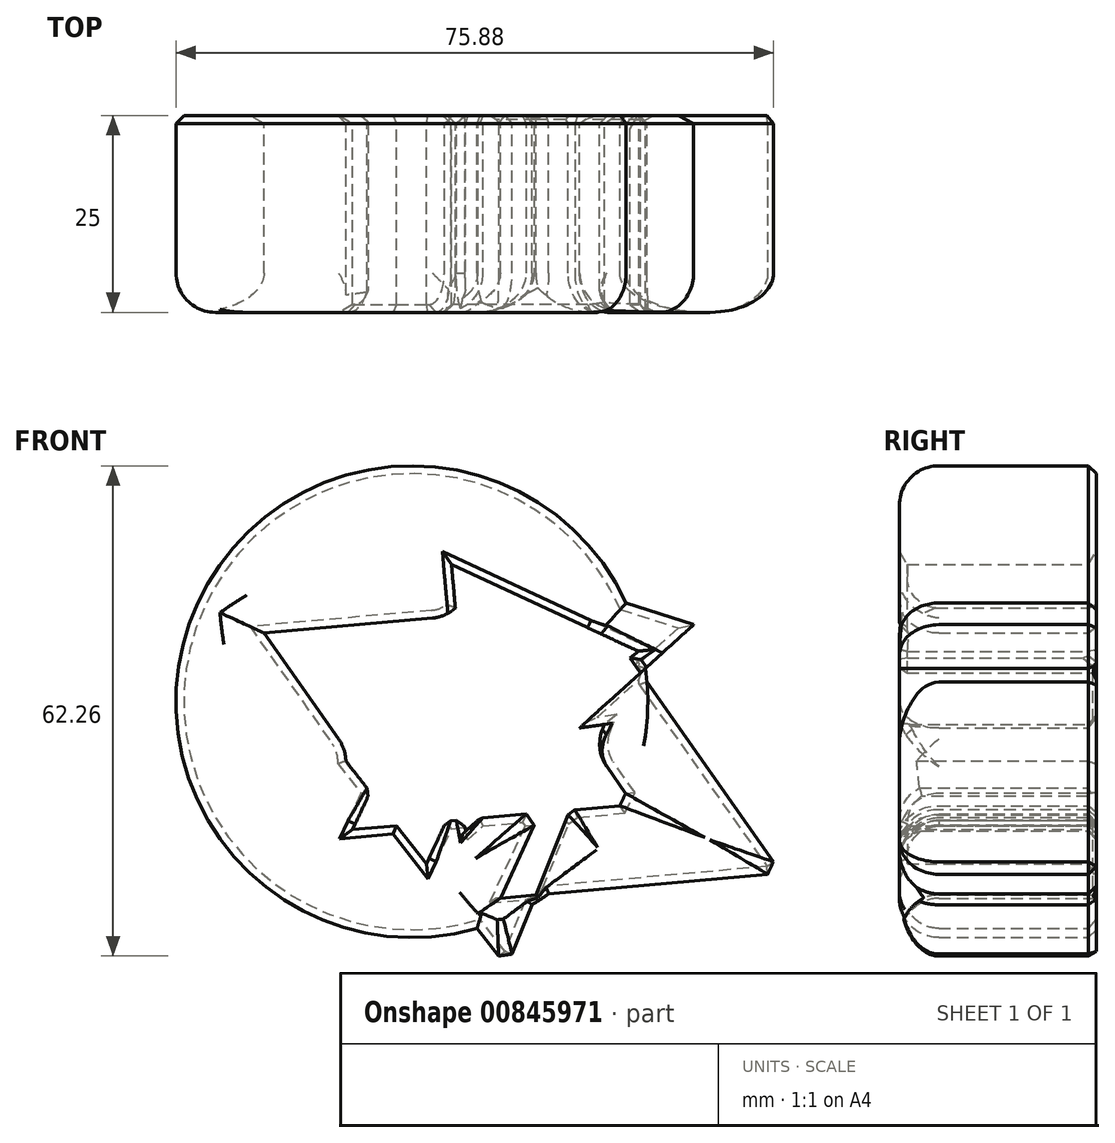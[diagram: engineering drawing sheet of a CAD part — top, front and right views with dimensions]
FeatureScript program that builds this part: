
annotation { "Feature Type Name" : "Feature", "Feature Type Description" : "" }
export const myFeature = defineFeature(function(context is Context, id is Id, definition is map)
    precondition{}
    {
        {
            var Q0;
            Q0=qCreatedBy(makeId("Front.planeOp"),FACE);
            var sketch = newSketch(context, id + "F0", { "sketchPlane" : qUnion([Q0])});
            skCircle(sketch, "E0", {"center": v(0, 0) * mm, "radius": 29.96 * mm});
            skCircle(sketch, "E1.cCircle", {"center": v(0, 0) * mm, "radius": 10.34 * mm, "construction": true});
            skLineSegment(sketch, "E1.0", {"start": v(16.92, 11.9) * mm, "end": v(1.84, -20.6) * mm});
            skLineSegment(sketch, "E1.1", {"start": v(1.84, -20.6) * mm, "end": v(-18.77, 8.7) * mm});
            skLineSegment(sketch, "E1.2", {"start": v(-18.77, 8.7) * mm, "end": v(16.92, 11.9) * mm});
            skPoint(sketch, "E1.0.midPoint", {"position": v(9.38, -4.35) * mm});
            skCircle(sketch, "E2.cCircle", {"center": v(9.38, -4.35) * mm, "radius": 10.34 * mm, "construction": true});
            skLineSegment(sketch, "E2.0", {"start": v(-7.54, -16.25) * mm, "end": v(7.54, 16.25) * mm});
            skLineSegment(sketch, "E2.1", {"start": v(7.54, 16.25) * mm, "end": v(28.15, -13.06) * mm});
            skLineSegment(sketch, "E2.2", {"start": v(28.15, -13.06) * mm, "end": v(-7.54, -16.25) * mm});
            skCircle(sketch, "E3.cCircle", {"center": v(28.15, -13.06) * mm, "radius": 10.34 * mm, "construction": true});
            skLineSegment(sketch, "E3.0", {"start": v(11.23, -24.96) * mm, "end": v(26.3, 7.55) * mm});
            skLineSegment(sketch, "E3.1", {"start": v(26.3, 7.55) * mm, "end": v(46.92, -21.77) * mm});
            skLineSegment(sketch, "E3.2", {"start": v(46.92, -21.77) * mm, "end": v(11.23, -24.96) * mm});
            skPoint(sketch, "E3.0.midPoint", {"position": v(18.77, -8.7) * mm});
            skCircle(sketch, "E4.cCircle", {"center": v(9.38, -14.7) * mm, "radius": 9.58 * mm, "construction": true});
            skLineSegment(sketch, "E4.0", {"start": v(12.08, -33.67) * mm, "end": v(-8.4, -7.55) * mm});
            skLineSegment(sketch, "E4.1", {"start": v(-8.4, -7.55) * mm, "end": v(24.47, -2.88) * mm});
            skLineSegment(sketch, "E4.2", {"start": v(24.47, -2.88) * mm, "end": v(12.08, -33.67) * mm});
            skPoint(sketch, "E4.0.midPoint", {"position": v(1.84, -20.6) * mm});
            skCircle(sketch, "E5.cCircle", {"center": v(13.74, 5.03) * mm, "radius": 7.57 * mm, "construction": true});
            skLineSegment(sketch, "E5.0", {"start": v(5.03, 17.42) * mm, "end": v(28.82, 6.38) * mm});
            skLineSegment(sketch, "E5.1", {"start": v(28.82, 6.38) * mm, "end": v(7.36, -8.7) * mm});
            skLineSegment(sketch, "E5.2", {"start": v(7.36, -8.7) * mm, "end": v(5.03, 17.42) * mm});
            skPoint(sketch, "E5.0.midPoint", {"position": v(16.92, 11.9) * mm});
            skCircle(sketch, "E6.cCircle", {"center": v(13.74, 5.03) * mm, "radius": 11.28 * mm, "construction": true});
            skLineSegment(sketch, "E6.0", {"start": v(35.79, 9.79) * mm, "end": v(6.83, -16.44) * mm});
            skLineSegment(sketch, "E6.1", {"start": v(6.83, -16.44) * mm, "end": v(-1.4, 21.75) * mm});
            skLineSegment(sketch, "E6.2", {"start": v(-1.4, 21.75) * mm, "end": v(35.79, 9.79) * mm});
            skPoint(sketch, "E6.0.midPoint", {"position": v(21.3, -3.33) * mm});
            skSolve(sketch);
        }
        {
            var Q0;
            Q0 = qSketchRegion(id + "F0", true);
            extrude(context, id + "F1", {"entities" : qUnion([Q0]), "depth" : 25 * mm, "offsetDistance" : 25 * mm});
        }
        {
            var Q0;
            {var subQ0=sQuery(id+"F0.wireOp",EDGE,"E0");Q0=makeQuery(id+"F1.opExtrude","CAP_EDGE",EDGE,{"disambiguationData":[OSD([subQ0]),TDD([makeQuery(id+"F0.imprint","IMPRINT",EDGE,{"disambiguationData":[TD([[makeQuery(id+"F0.imprint","INTERSECT",VERTEX,{"derivedFrom":[subQ0,sQuery(id+"F0.wireOp",EDGE,"E6.2")]}),-1.0]])],"derivedFrom":subQ0})])],"isStart":false});}
            var Q1;
            {var subQ0=sQuery(id+"F0.wireOp",EDGE,"E3.2");Q1=makeQuery(id+"F1.opExtrude","CAP_EDGE",EDGE,{"disambiguationData":[OSD([subQ0]),TDD([makeQuery(id+"F0.imprint","IMPRINT",EDGE,{"disambiguationData":[TD([[makeQuery(id+"F0.imprint","INTERSECT",VERTEX,{"derivedFrom":[sQuery(id+"F0.wireOp",EDGE,"E3.1"),subQ0]}),-1.0]])],"derivedFrom":subQ0})])],"isStart":false});}
            var Q2;
            {var subQ0=sQuery(id+"F0.wireOp",EDGE,"E4.2");Q2=makeQuery(id+"F1.opExtrude","CAP_EDGE",EDGE,{"disambiguationData":[OSD([subQ0]),TDD([makeQuery(id+"F0.imprint","IMPRINT",EDGE,{"disambiguationData":[TD([[makeQuery(id+"F0.imprint","INTERSECT",VERTEX,{"derivedFrom":[sQuery(id+"F0.wireOp",EDGE,"E4.0"),subQ0]}),1.0]])],"derivedFrom":subQ0})])],"isStart":false});}
            var Q3;
            {var subQ0=sQuery(id+"F0.wireOp",EDGE,"E0");Q3=makeQuery(id+"F1.opExtrude","CAP_EDGE",EDGE,{"disambiguationData":[OSD([subQ0]),TDD([makeQuery(id+"F0.imprint","IMPRINT",EDGE,{"disambiguationData":[TD([[makeQuery(id+"F0.imprint","INTERSECT",VERTEX,{"derivedFrom":[subQ0,sQuery(id+"F0.wireOp",EDGE,"E4.2")]}),-1.0]])],"derivedFrom":subQ0})])],"isStart":false});}
            var Q4;
            {var subQ0=sQuery(id+"F0.wireOp",EDGE,"E4.0");Q4=makeQuery(id+"F1.opExtrude","CAP_EDGE",EDGE,{"disambiguationData":[OSD([subQ0]),TDD([makeQuery(id+"F0.imprint","IMPRINT",EDGE,{"disambiguationData":[TD([[makeQuery(id+"F0.imprint","INTERSECT",VERTEX,{"derivedFrom":[subQ0,sQuery(id+"F0.wireOp",EDGE,"E4.2")]}),-1.0]])],"derivedFrom":subQ0})])],"isStart":false});}
            var Q5;
            Q5=makeQuery(id+"F1.opExtrude","CAP_EDGE",EDGE,{"disambiguationData":[OSD([sQuery(id+"F0.wireOp",EDGE,"E6.2")])],"isStart":false});
            var Q6;
            {var subQ0=sQuery(id+"F0.wireOp",EDGE,"E3.1");Q6=makeQuery(id+"F1.opExtrude","CAP_EDGE",EDGE,{"disambiguationData":[OSD([subQ0]),TDD([makeQuery(id+"F0.imprint","IMPRINT",EDGE,{"disambiguationData":[TD([[makeQuery(id+"F0.imprint","INTERSECT",VERTEX,{"derivedFrom":[subQ0,sQuery(id+"F0.wireOp",EDGE,"E3.2")]}),1.0]])],"derivedFrom":subQ0})])],"isStart":false});}
            var Q7;
            Q7=makeQuery(id+"F1.opExtrude","CAP_EDGE",EDGE,{"disambiguationData":[OSD([sQuery(id+"F0.wireOp",EDGE,"E1.1")])],"isStart":false});
            var Q8;
            Q8=makeQuery(id+"F1.opExtrude","CAP_EDGE",EDGE,{"disambiguationData":[OSD([sQuery(id+"F0.wireOp",EDGE,"E1.2")])],"isStart":false});
            var Q9;
            Q9=makeQuery(id+"F1.opExtrude","SWEPT_EDGE",EDGE,{"disambiguationData":[OSD([sQuery(id+"F0.wireOp",EDGE,"E1.2"),sQuery(id+"F0.wireOp",EDGE,"E2.0")])]});
            var Q10;
            Q10=makeQuery(id+"F1.opExtrude","SWEPT_EDGE",EDGE,{"disambiguationData":[OSD([sQuery(id+"F0.wireOp",EDGE,"E1.1"),sQuery(id+"F0.wireOp",EDGE,"E4.1")])]});
            var Q11;
            Q11=makeQuery(id+"F1.opExtrude","SWEPT_EDGE",EDGE,{"disambiguationData":[OSD([sQuery(id+"F0.wireOp",EDGE,"E2.1"),sQuery(id+"F0.wireOp",EDGE,"E4.2")])]});
            var Q12;
            Q12=makeQuery(id+"F1.opExtrude","CAP_EDGE",EDGE,{"disambiguationData":[OSD([sQuery(id+"F0.wireOp",EDGE,"E2.1")])],"isStart":false});
            var Q13;
            {var subQ0=sQuery(id+"F0.wireOp",EDGE,"E2.2");var subQ1=makeQuery(id+"F0.imprint","INTERSECT",VERTEX,{"derivedFrom":[sQuery(id+"F0.wireOp",EDGE,"E0"),subQ0]});Q13=makeQuery(id+"F1.opExtrude","CAP_EDGE",EDGE,{"disambiguationData":[OSD([subQ0]),TDD([makeQuery(id+"F0.imprint","IMPRINT",EDGE,{"disambiguationData":[TD([[makeQuery(id+"F0.imprint","INTERSECT",VERTEX,{"derivedFrom":[sQuery(id+"F0.wireOp",EDGE,"E2.1"),subQ0]}),-1.0]])],"derivedFrom":subQ0}),makeQuery(id+"F0.imprint","IMPRINT",EDGE,{"disambiguationData":[TD([[subQ1,-1.0]])],"derivedFrom":subQ0})])],"isStart":false});}
            var Q14;
            {var subQ0=sQuery(id+"F0.wireOp",EDGE,"E4.2");Q14=makeQuery(id+"F1.opExtrude","CAP_EDGE",EDGE,{"disambiguationData":[OSD([subQ0]),TDD([makeQuery(id+"F0.imprint","IMPRINT",EDGE,{"disambiguationData":[TD([[makeQuery(id+"F0.imprint","INTERSECT",VERTEX,{"derivedFrom":[sQuery(id+"F0.wireOp",EDGE,"E2.2"),subQ0]}),-1.0]])],"derivedFrom":subQ0})])],"isStart":false});}
            var Q15;
            {var subQ0=sQuery(id+"F0.wireOp",EDGE,"E3.2");Q15=makeQuery(id+"F1.opExtrude","CAP_EDGE",EDGE,{"disambiguationData":[OSD([subQ0]),TDD([makeQuery(id+"F0.imprint","IMPRINT",EDGE,{"disambiguationData":[TD([[makeQuery(id+"F0.imprint","INTERSECT",VERTEX,{"derivedFrom":[sQuery(id+"F0.wireOp",EDGE,"E3.0"),subQ0]}),1.0]])],"derivedFrom":subQ0})])],"isStart":false});}
            var Q16;
            Q16=makeQuery(id+"F1.opExtrude","CAP_EDGE",EDGE,{"disambiguationData":[OSD([sQuery(id+"F0.wireOp",EDGE,"E3.0")])],"isStart":false});
            var Q17;
            {var subQ0=sQuery(id+"F0.wireOp",EDGE,"E2.2");Q17=makeQuery(id+"F1.opExtrude","CAP_EDGE",EDGE,{"disambiguationData":[OSD([subQ0]),TDD([makeQuery(id+"F0.imprint","IMPRINT",EDGE,{"disambiguationData":[TD([[makeQuery(id+"F0.imprint","INTERSECT",VERTEX,{"derivedFrom":[subQ0,sQuery(id+"F0.wireOp",EDGE,"E3.0")]}),-1.0]])],"derivedFrom":subQ0})])],"isStart":false});}
            fillet(context, id + "F2", {"entities" : qUnion([Q0, Q1, Q2, Q3, Q4, Q5, Q6, Q7, Q8, Q9, Q10, Q11, Q12, Q13, Q14, Q15, Q16, Q17]), "radius" : 5 * mm, "tangentPropagation" : true, "allowEdgeOverflow" : false});
        }
        {
            var Q0;
            Q0=makeQuery(id+"F1.opExtrude","CAP_EDGE",EDGE,{"disambiguationData":[OSD([sQuery(id+"F0.wireOp",EDGE,"E5.0")])],"isStart":false});
            var Q1;
            Q1=makeQuery(id+"F1.opExtrude","CAP_EDGE",EDGE,{"disambiguationData":[OSD([sQuery(id+"F0.wireOp",EDGE,"E5.1")])],"isStart":false});
            var Q2;
            {var subQ0=sQuery(id+"F0.wireOp",EDGE,"E3.1");Q2=makeQuery(id+"F1.opExtrude","CAP_EDGE",EDGE,{"disambiguationData":[OSD([subQ0]),TDD([makeQuery(id+"F0.imprint","IMPRINT",EDGE,{"disambiguationData":[TD([[makeQuery(id+"F0.imprint","INTERSECT",VERTEX,{"derivedFrom":[subQ0,sQuery(id+"F0.wireOp",EDGE,"E5.1")]}),-1.0]])],"derivedFrom":subQ0})])],"isStart":false});}
            var Q3;
            Q3=makeQuery(id+"F2.opFillet","BLEND_EDGE",EDGE,{"blendedFrom":[makeQuery(id+"F1.opExtrude","CAP_EDGE",EDGE,{"disambiguationData":[OSD([sQuery(id+"F0.wireOp",EDGE,"E1.2")])],"isStart":false}),makeQuery(id+"F1.opExtrude","SWEPT_FACE",FACE,{"disambiguationData":[OSD([sQuery(id+"F0.wireOp",EDGE,"E5.2")])]})],"blendedInto":[makeQuery(id+"F1.opExtrude","SWEPT_FACE",FACE,{"disambiguationData":[OSD([sQuery(id+"F0.wireOp",EDGE,"E5.2")])]})]});
            var Q4;
            Q4=makeQuery(id+"F1.opExtrude","CAP_EDGE",EDGE,{"disambiguationData":[OSD([sQuery(id+"F0.wireOp",EDGE,"E5.2")])],"isStart":false});
            var Q5;
            {var subQ0=sQuery(id+"F0.wireOp",EDGE,"E2.2");Q5=makeQuery(id+"F1.opExtrude","CAP_EDGE",EDGE,{"disambiguationData":[OSD([subQ0]),TDD([makeQuery(id+"F0.imprint","IMPRINT",EDGE,{"disambiguationData":[TD([[makeQuery(id+"F0.imprint","INTERSECT",VERTEX,{"derivedFrom":[sQuery(id+"F0.wireOp",EDGE,"E2.0"),subQ0]}),1.0]])],"derivedFrom":subQ0})])],"isStart":false});}
            var Q6;
            {var subQ0=sQuery(id+"F0.wireOp",EDGE,"E2.0");Q6=makeQuery(id+"F2.opFillet","BLEND_EDGE",EDGE,{"blendedFrom":[makeQuery(id+"F1.opExtrude","CAP_EDGE",EDGE,{"disambiguationData":[OSD([sQuery(id+"F0.wireOp",EDGE,"E1.1")])],"isStart":false}),makeQuery(id+"F1.opExtrude","SWEPT_FACE",FACE,{"disambiguationData":[OSD([subQ0]),TDD([makeQuery(id+"F0.imprint","IMPRINT",EDGE,{"disambiguationData":[TD([[makeQuery(id+"F0.imprint","INTERSECT",VERTEX,{"derivedFrom":[subQ0,sQuery(id+"F0.wireOp",EDGE,"E2.2")]}),-1.0]])],"derivedFrom":subQ0})])]})],"blendedInto":[makeQuery(id+"F1.opExtrude","SWEPT_FACE",FACE,{"disambiguationData":[OSD([subQ0]),TDD([makeQuery(id+"F0.imprint","IMPRINT",EDGE,{"disambiguationData":[TD([[makeQuery(id+"F0.imprint","INTERSECT",VERTEX,{"derivedFrom":[subQ0,sQuery(id+"F0.wireOp",EDGE,"E2.2")]}),-1.0]])],"derivedFrom":subQ0})])]})]});}
            var Q7;
            {var subQ0=sQuery(id+"F0.wireOp",EDGE,"E4.0");Q7=makeQuery(id+"F1.opExtrude","CAP_EDGE",EDGE,{"disambiguationData":[OSD([subQ0]),TDD([makeQuery(id+"F0.imprint","IMPRINT",EDGE,{"disambiguationData":[TD([[makeQuery(id+"F0.imprint","INTERSECT",VERTEX,{"derivedFrom":[sQuery(id+"F0.wireOp",EDGE,"E2.2"),subQ0]}),1.0]])],"derivedFrom":subQ0})])],"isStart":false});}
            var Q8;
            {var subQ0=sQuery(id+"F0.wireOp",EDGE,"E2.2");Q8=makeQuery(id+"F2.opFillet","BLEND_EDGE",EDGE,{"blendedFrom":[makeQuery(id+"F1.opExtrude","CAP_EDGE",EDGE,{"disambiguationData":[OSD([subQ0]),TDD([makeQuery(id+"F0.imprint","IMPRINT",EDGE,{"disambiguationData":[TD([[makeQuery(id+"F0.imprint","INTERSECT",VERTEX,{"derivedFrom":[subQ0,sQuery(id+"F0.wireOp",EDGE,"E3.0")]}),-1.0]])],"derivedFrom":subQ0})])],"isStart":false}),makeQuery(id+"F1.opExtrude","SWEPT_FACE",FACE,{"disambiguationData":[OSD([sQuery(id+"F0.wireOp",EDGE,"E1.0")])]})],"blendedInto":[makeQuery(id+"F1.opExtrude","SWEPT_FACE",FACE,{"disambiguationData":[OSD([sQuery(id+"F0.wireOp",EDGE,"E1.0")])]})]});}
            var Q9;
            {var subQ0=sQuery(id+"F0.wireOp",EDGE,"E6.0");var subQ1=sQuery(id+"F0.wireOp",EDGE,"E2.2");Q9=makeQuery(id+"F2.opFillet","BLEND_EDGE",EDGE,{"blendedFrom":[makeQuery(id+"F1.opExtrude","CAP_EDGE",EDGE,{"disambiguationData":[OSD([subQ1]),TDD([makeQuery(id+"F0.imprint","IMPRINT",EDGE,{"disambiguationData":[TD([[makeQuery(id+"F0.imprint","INTERSECT",VERTEX,{"derivedFrom":[subQ1,sQuery(id+"F0.wireOp",EDGE,"E3.0")]}),-1.0]])],"derivedFrom":subQ1})])],"isStart":false}),makeQuery(id+"F1.opExtrude","SWEPT_FACE",FACE,{"disambiguationData":[OSD([subQ0]),TDD([makeQuery(id+"F0.imprint","IMPRINT",EDGE,{"disambiguationData":[TD([[makeQuery(id+"F0.imprint","INTERSECT",VERTEX,{"derivedFrom":[subQ0,sQuery(id+"F0.wireOp",EDGE,"E6.1")]}),1.0]])],"derivedFrom":subQ0})])]})],"blendedInto":[makeQuery(id+"F1.opExtrude","SWEPT_FACE",FACE,{"disambiguationData":[OSD([subQ0]),TDD([makeQuery(id+"F0.imprint","IMPRINT",EDGE,{"disambiguationData":[TD([[makeQuery(id+"F0.imprint","INTERSECT",VERTEX,{"derivedFrom":[subQ0,sQuery(id+"F0.wireOp",EDGE,"E6.1")]}),1.0]])],"derivedFrom":subQ0})])]})]});}
            var Q10;
            {var subQ0=sQuery(id+"F0.wireOp",EDGE,"E2.2");Q10=makeQuery(id+"F2.opFillet","BLEND_EDGE",EDGE,{"blendedFrom":[makeQuery(id+"F1.opExtrude","CAP_EDGE",EDGE,{"disambiguationData":[OSD([subQ0]),TDD([makeQuery(id+"F0.imprint","IMPRINT",EDGE,{"disambiguationData":[TD([[makeQuery(id+"F0.imprint","INTERSECT",VERTEX,{"derivedFrom":[subQ0,sQuery(id+"F0.wireOp",EDGE,"E3.0")]}),-1.0]])],"derivedFrom":subQ0})])],"isStart":false}),makeQuery(id+"F1.opExtrude","SWEPT_FACE",FACE,{"disambiguationData":[OSD([sQuery(id+"F0.wireOp",EDGE,"E6.1")])]})],"blendedInto":[makeQuery(id+"F1.opExtrude","SWEPT_FACE",FACE,{"disambiguationData":[OSD([sQuery(id+"F0.wireOp",EDGE,"E6.1")])]})]});}
            var Q11;
            Q11=makeQuery(id+"F1.opExtrude","SWEPT_EDGE",EDGE,{"disambiguationData":[OSD([sQuery(id+"F0.wireOp",EDGE,"E2.2"),sQuery(id+"F0.wireOp",EDGE,"E3.0")])]});
            var Q12;
            {var subQ0=sQuery(id+"F0.wireOp",EDGE,"E3.0");var subQ1=sQuery(id+"F0.wireOp",EDGE,"E2.2");Q12=makeQuery(id+"F2.opFillet","BLEND_EDGE",EDGE,{"blendedFrom":[makeQuery(id+"F1.opExtrude","CAP_EDGE",EDGE,{"disambiguationData":[OSD([subQ1]),TDD([makeQuery(id+"F0.imprint","IMPRINT",EDGE,{"disambiguationData":[TD([[makeQuery(id+"F0.imprint","INTERSECT",VERTEX,{"derivedFrom":[subQ1,subQ0]}),-1.0]])],"derivedFrom":subQ1})])],"isStart":false}),makeQuery(id+"F1.opExtrude","CAP_EDGE",EDGE,{"disambiguationData":[OSD([subQ0])],"isStart":false})],"blendedInto":[]});}
            var Q13;
            Q13=makeQuery(id+"F1.opExtrude","SWEPT_EDGE",EDGE,{"disambiguationData":[OSD([sQuery(id+"F0.wireOp",EDGE,"E2.2"),sQuery(id+"F0.wireOp",EDGE,"E4.2")])]});
            var Q14;
            {var subQ0=sQuery(id+"F0.wireOp",EDGE,"E4.2");var subQ1=sQuery(id+"F0.wireOp",EDGE,"E2.2");var subQ2=makeQuery(id+"F0.imprint","INTERSECT",VERTEX,{"derivedFrom":[subQ1,subQ0]});var subQ3=makeQuery(id+"F0.imprint","INTERSECT",VERTEX,{"derivedFrom":[sQuery(id+"F0.wireOp",EDGE,"E0"),subQ1]});Q14=makeQuery(id+"F2.opFillet","BLEND_EDGE",EDGE,{"blendedFrom":[makeQuery(id+"F1.opExtrude","CAP_EDGE",EDGE,{"disambiguationData":[OSD([subQ1]),TDD([makeQuery(id+"F0.imprint","IMPRINT",EDGE,{"disambiguationData":[TD([[makeQuery(id+"F0.imprint","INTERSECT",VERTEX,{"derivedFrom":[sQuery(id+"F0.wireOp",EDGE,"E2.1"),subQ1]}),-1.0]])],"derivedFrom":subQ1}),makeQuery(id+"F0.imprint","IMPRINT",EDGE,{"disambiguationData":[TD([[subQ3,-1.0]])],"derivedFrom":subQ1})])],"isStart":false}),makeQuery(id+"F1.opExtrude","CAP_EDGE",EDGE,{"disambiguationData":[OSD([subQ0]),TDD([makeQuery(id+"F0.imprint","IMPRINT",EDGE,{"disambiguationData":[TD([[subQ2,-1.0]])],"derivedFrom":subQ0})])],"isStart":false})],"blendedInto":[]});}
            var Q15;
            Q15=makeQuery(id+"F1.opExtrude","SWEPT_EDGE",EDGE,{"disambiguationData":[OSD([sQuery(id+"F0.wireOp",EDGE,"E2.1"),sQuery(id+"F0.wireOp",EDGE,"E2.2")])]});
            var Q16;
            {var subQ0=sQuery(id+"F0.wireOp",EDGE,"E2.1");Q16=makeQuery(id+"F2.opFillet","BLEND_EDGE",EDGE,{"blendedFrom":[makeQuery(id+"F1.opExtrude","SWEPT_EDGE",EDGE,{"disambiguationData":[OSD([subQ0,sQuery(id+"F0.wireOp",EDGE,"E4.2")])]}),makeQuery(id+"F1.opExtrude","CAP_EDGE",EDGE,{"disambiguationData":[OSD([subQ0])],"isStart":false})],"blendedInto":[]});}
            var Q17;
            Q17=makeQuery(id+"F1.opExtrude","SWEPT_EDGE",EDGE,{"disambiguationData":[OSD([sQuery(id+"F0.wireOp",EDGE,"E2.0"),sQuery(id+"F0.wireOp",EDGE,"E4.0")])]});
            var Q18;
            {var subQ0=sQuery(id+"F0.wireOp",EDGE,"E1.1");Q18=makeQuery(id+"F2.opFillet","BLEND_EDGE",EDGE,{"blendedFrom":[makeQuery(id+"F1.opExtrude","SWEPT_EDGE",EDGE,{"disambiguationData":[OSD([subQ0,sQuery(id+"F0.wireOp",EDGE,"E4.1")])]}),makeQuery(id+"F1.opExtrude","SWEPT_FACE",FACE,{"disambiguationData":[OSD([subQ0])]})],"blendedInto":[makeQuery(id+"F1.opExtrude","SWEPT_FACE",FACE,{"disambiguationData":[OSD([subQ0])]})]});}
            chamfer(context, id + "F3", {"entities" : qUnion([Q0, Q1, Q2, Q3, Q4, Q5, Q6, Q7, Q8, Q9, Q10, Q11, Q12, Q13, Q14, Q15, Q16, Q17, Q18]), "width" : 1 * mm, "tangentPropagation" : true});
        }
        {
            var Q0;
            {var subQ0=sQuery(id+"F0.wireOp",EDGE,"E0");Q0=makeQuery(id+"F1.opExtrude","CAP_EDGE",EDGE,{"disambiguationData":[OSD([subQ0]),TDD([makeQuery(id+"F0.imprint","IMPRINT",EDGE,{"disambiguationData":[TD([[makeQuery(id+"F0.imprint","INTERSECT",VERTEX,{"derivedFrom":[subQ0,sQuery(id+"F0.wireOp",EDGE,"E6.2")]}),-1.0]])],"derivedFrom":subQ0})])],"isStart":true});}
            var Q1;
            {var subQ0=sQuery(id+"F0.wireOp",EDGE,"E3.1");Q1=makeQuery(id+"F1.opExtrude","CAP_EDGE",EDGE,{"disambiguationData":[OSD([subQ0]),TDD([makeQuery(id+"F0.imprint","IMPRINT",EDGE,{"disambiguationData":[TD([[makeQuery(id+"F0.imprint","INTERSECT",VERTEX,{"derivedFrom":[subQ0,sQuery(id+"F0.wireOp",EDGE,"E3.2")]}),1.0]])],"derivedFrom":subQ0})])],"isStart":true});}
            var Q2;
            {var subQ0=sQuery(id+"F0.wireOp",EDGE,"E3.2");Q2=makeQuery(id+"F1.opExtrude","CAP_EDGE",EDGE,{"disambiguationData":[OSD([subQ0]),TDD([makeQuery(id+"F0.imprint","IMPRINT",EDGE,{"disambiguationData":[TD([[makeQuery(id+"F0.imprint","INTERSECT",VERTEX,{"derivedFrom":[sQuery(id+"F0.wireOp",EDGE,"E3.1"),subQ0]}),-1.0]])],"derivedFrom":subQ0})])],"isStart":true});}
            var Q3;
            {var subQ0=sQuery(id+"F0.wireOp",EDGE,"E0");Q3=makeQuery(id+"F1.opExtrude","CAP_EDGE",EDGE,{"disambiguationData":[OSD([subQ0]),TDD([makeQuery(id+"F0.imprint","IMPRINT",EDGE,{"disambiguationData":[TD([[makeQuery(id+"F0.imprint","INTERSECT",VERTEX,{"derivedFrom":[subQ0,sQuery(id+"F0.wireOp",EDGE,"E4.2")]}),-1.0]])],"derivedFrom":subQ0})])],"isStart":true});}
            var Q4;
            {var subQ0=sQuery(id+"F0.wireOp",EDGE,"E4.2");Q4=makeQuery(id+"F1.opExtrude","CAP_EDGE",EDGE,{"disambiguationData":[OSD([subQ0]),TDD([makeQuery(id+"F0.imprint","IMPRINT",EDGE,{"disambiguationData":[TD([[makeQuery(id+"F0.imprint","INTERSECT",VERTEX,{"derivedFrom":[sQuery(id+"F0.wireOp",EDGE,"E4.0"),subQ0]}),1.0]])],"derivedFrom":subQ0})])],"isStart":true});}
            var Q5;
            {var subQ0=sQuery(id+"F0.wireOp",EDGE,"E4.0");Q5=makeQuery(id+"F1.opExtrude","CAP_EDGE",EDGE,{"disambiguationData":[OSD([subQ0]),TDD([makeQuery(id+"F0.imprint","IMPRINT",EDGE,{"disambiguationData":[TD([[makeQuery(id+"F0.imprint","INTERSECT",VERTEX,{"derivedFrom":[subQ0,sQuery(id+"F0.wireOp",EDGE,"E4.2")]}),-1.0]])],"derivedFrom":subQ0})])],"isStart":true});}
            var Q6;
            Q6=makeQuery(id+"F1.opExtrude","CAP_EDGE",EDGE,{"disambiguationData":[OSD([sQuery(id+"F0.wireOp",EDGE,"E6.2")])],"isStart":true});
            var Q7;
            {var subQ0=sQuery(id+"F0.wireOp",EDGE,"E6.0");Q7=makeQuery(id+"F1.opExtrude","CAP_EDGE",EDGE,{"disambiguationData":[OSD([subQ0]),TDD([makeQuery(id+"F0.imprint","IMPRINT",EDGE,{"disambiguationData":[TD([[makeQuery(id+"F0.imprint","INTERSECT",VERTEX,{"derivedFrom":[subQ0,sQuery(id+"F0.wireOp",EDGE,"E6.2")]}),-1.0]])],"derivedFrom":subQ0})])],"isStart":true});}
            var Q8;
            {var subQ0=sQuery(id+"F0.wireOp",EDGE,"E0");Q8=makeQuery(id+"F1.opExtrude","CAP_EDGE",EDGE,{"disambiguationData":[OSD([subQ0]),TDD([makeQuery(id+"F0.imprint","IMPRINT",EDGE,{"disambiguationData":[TD([[makeQuery(id+"F0.imprint","INTERSECT",VERTEX,{"derivedFrom":[subQ0,sQuery(id+"F0.wireOp",EDGE,"E6.0")]}),1.0]])],"derivedFrom":subQ0})])],"isStart":true});}
            var Q9;
            Q9=makeQuery(id+"F1.opExtrude","CAP_EDGE",EDGE,{"disambiguationData":[OSD([sQuery(id+"F0.wireOp",EDGE,"E5.0")])],"isStart":true});
            var Q10;
            Q10=makeQuery(id+"F1.opExtrude","CAP_EDGE",EDGE,{"disambiguationData":[OSD([sQuery(id+"F0.wireOp",EDGE,"E5.2")])],"isStart":true});
            var Q11;
            Q11=makeQuery(id+"F1.opExtrude","CAP_EDGE",EDGE,{"disambiguationData":[OSD([sQuery(id+"F0.wireOp",EDGE,"E1.2")])],"isStart":true});
            var Q12;
            {var subQ0=sQuery(id+"F0.wireOp",EDGE,"E2.0");var subQ1=sQuery(id+"F0.wireOp",EDGE,"E1.2");Q12=makeQuery(id+"F2.opFillet","BLEND_EDGE",EDGE,{"blendedFrom":[makeQuery(id+"F1.opExtrude","SWEPT_EDGE",EDGE,{"disambiguationData":[OSD([subQ1,subQ0])]}),makeQuery(id+"F1.opExtrude","CAP_FACE",FACE,{"disambiguationData":[OSD([sQuery(id+"F0.wireOp",EDGE,"E0"),sQuery(id+"F0.wireOp",EDGE,"E1.0"),sQuery(id+"F0.wireOp",EDGE,"E1.1"),subQ1,subQ0,sQuery(id+"F0.wireOp",EDGE,"E2.1"),sQuery(id+"F0.wireOp",EDGE,"E2.2"),sQuery(id+"F0.wireOp",EDGE,"E3.0"),sQuery(id+"F0.wireOp",EDGE,"E3.1"),sQuery(id+"F0.wireOp",EDGE,"E3.2"),sQuery(id+"F0.wireOp",EDGE,"E4.0"),sQuery(id+"F0.wireOp",EDGE,"E4.1"),sQuery(id+"F0.wireOp",EDGE,"E4.2"),sQuery(id+"F0.wireOp",EDGE,"E5.0"),sQuery(id+"F0.wireOp",EDGE,"E5.1"),sQuery(id+"F0.wireOp",EDGE,"E5.2"),sQuery(id+"F0.wireOp",EDGE,"E6.0"),sQuery(id+"F0.wireOp",EDGE,"E6.1"),sQuery(id+"F0.wireOp",EDGE,"E6.2")])],"isStart":true})],"blendedInto":[makeQuery(id+"F1.opExtrude","CAP_FACE",FACE,{"disambiguationData":[OSD([sQuery(id+"F0.wireOp",EDGE,"E0"),sQuery(id+"F0.wireOp",EDGE,"E1.0"),sQuery(id+"F0.wireOp",EDGE,"E1.1"),subQ1,subQ0,sQuery(id+"F0.wireOp",EDGE,"E2.1"),sQuery(id+"F0.wireOp",EDGE,"E2.2"),sQuery(id+"F0.wireOp",EDGE,"E3.0"),sQuery(id+"F0.wireOp",EDGE,"E3.1"),sQuery(id+"F0.wireOp",EDGE,"E3.2"),sQuery(id+"F0.wireOp",EDGE,"E4.0"),sQuery(id+"F0.wireOp",EDGE,"E4.1"),sQuery(id+"F0.wireOp",EDGE,"E4.2"),sQuery(id+"F0.wireOp",EDGE,"E5.0"),sQuery(id+"F0.wireOp",EDGE,"E5.1"),sQuery(id+"F0.wireOp",EDGE,"E5.2"),sQuery(id+"F0.wireOp",EDGE,"E6.0"),sQuery(id+"F0.wireOp",EDGE,"E6.1"),sQuery(id+"F0.wireOp",EDGE,"E6.2")])],"isStart":true})]});}
            var Q13;
            Q13=makeQuery(id+"F1.opExtrude","CAP_EDGE",EDGE,{"disambiguationData":[OSD([sQuery(id+"F0.wireOp",EDGE,"E1.1")])],"isStart":true});
            var Q14;
            {var subQ0=sQuery(id+"F0.wireOp",EDGE,"E4.0");Q14=makeQuery(id+"F1.opExtrude","CAP_EDGE",EDGE,{"disambiguationData":[OSD([subQ0]),TDD([makeQuery(id+"F0.imprint","IMPRINT",EDGE,{"disambiguationData":[TD([[makeQuery(id+"F0.imprint","INTERSECT",VERTEX,{"derivedFrom":[subQ0,sQuery(id+"F0.wireOp",EDGE,"E4.1")]}),1.0]])],"derivedFrom":subQ0})])],"isStart":true});}
            var Q15;
            {var subQ0=sQuery(id+"F0.wireOp",EDGE,"E4.1");var subQ1=sQuery(id+"F0.wireOp",EDGE,"E1.1");Q15=makeQuery(id+"F2.opFillet","BLEND_EDGE",EDGE,{"blendedFrom":[makeQuery(id+"F1.opExtrude","SWEPT_EDGE",EDGE,{"disambiguationData":[OSD([subQ1,subQ0])]}),makeQuery(id+"F1.opExtrude","CAP_FACE",FACE,{"disambiguationData":[OSD([sQuery(id+"F0.wireOp",EDGE,"E0"),sQuery(id+"F0.wireOp",EDGE,"E1.0"),subQ1,sQuery(id+"F0.wireOp",EDGE,"E1.2"),sQuery(id+"F0.wireOp",EDGE,"E2.0"),sQuery(id+"F0.wireOp",EDGE,"E2.1"),sQuery(id+"F0.wireOp",EDGE,"E2.2"),sQuery(id+"F0.wireOp",EDGE,"E3.0"),sQuery(id+"F0.wireOp",EDGE,"E3.1"),sQuery(id+"F0.wireOp",EDGE,"E3.2"),sQuery(id+"F0.wireOp",EDGE,"E4.0"),subQ0,sQuery(id+"F0.wireOp",EDGE,"E4.2"),sQuery(id+"F0.wireOp",EDGE,"E5.0"),sQuery(id+"F0.wireOp",EDGE,"E5.1"),sQuery(id+"F0.wireOp",EDGE,"E5.2"),sQuery(id+"F0.wireOp",EDGE,"E6.0"),sQuery(id+"F0.wireOp",EDGE,"E6.1"),sQuery(id+"F0.wireOp",EDGE,"E6.2")])],"isStart":true})],"blendedInto":[makeQuery(id+"F1.opExtrude","CAP_FACE",FACE,{"disambiguationData":[OSD([sQuery(id+"F0.wireOp",EDGE,"E0"),sQuery(id+"F0.wireOp",EDGE,"E1.0"),subQ1,sQuery(id+"F0.wireOp",EDGE,"E1.2"),sQuery(id+"F0.wireOp",EDGE,"E2.0"),sQuery(id+"F0.wireOp",EDGE,"E2.1"),sQuery(id+"F0.wireOp",EDGE,"E2.2"),sQuery(id+"F0.wireOp",EDGE,"E3.0"),sQuery(id+"F0.wireOp",EDGE,"E3.1"),sQuery(id+"F0.wireOp",EDGE,"E3.2"),sQuery(id+"F0.wireOp",EDGE,"E4.0"),subQ0,sQuery(id+"F0.wireOp",EDGE,"E4.2"),sQuery(id+"F0.wireOp",EDGE,"E5.0"),sQuery(id+"F0.wireOp",EDGE,"E5.1"),sQuery(id+"F0.wireOp",EDGE,"E5.2"),sQuery(id+"F0.wireOp",EDGE,"E6.0"),sQuery(id+"F0.wireOp",EDGE,"E6.1"),sQuery(id+"F0.wireOp",EDGE,"E6.2")])],"isStart":true})]});}
            var Q16;
            {var subQ0=sQuery(id+"F0.wireOp",EDGE,"E2.0");Q16=makeQuery(id+"F1.opExtrude","CAP_EDGE",EDGE,{"disambiguationData":[OSD([subQ0]),TDD([makeQuery(id+"F0.imprint","IMPRINT",EDGE,{"disambiguationData":[TD([[makeQuery(id+"F0.imprint","INTERSECT",VERTEX,{"derivedFrom":[subQ0,sQuery(id+"F0.wireOp",EDGE,"E2.2")]}),-1.0]])],"derivedFrom":subQ0})])],"isStart":true});}
            var Q17;
            {var subQ0=sQuery(id+"F0.wireOp",EDGE,"E2.2");Q17=makeQuery(id+"F1.opExtrude","CAP_EDGE",EDGE,{"disambiguationData":[OSD([subQ0]),TDD([makeQuery(id+"F0.imprint","IMPRINT",EDGE,{"disambiguationData":[TD([[makeQuery(id+"F0.imprint","INTERSECT",VERTEX,{"derivedFrom":[sQuery(id+"F0.wireOp",EDGE,"E2.0"),subQ0]}),1.0]])],"derivedFrom":subQ0})])],"isStart":true});}
            var Q18;
            {var subQ0=sQuery(id+"F0.wireOp",EDGE,"E4.0");Q18=makeQuery(id+"F1.opExtrude","CAP_EDGE",EDGE,{"disambiguationData":[OSD([subQ0]),TDD([makeQuery(id+"F0.imprint","IMPRINT",EDGE,{"disambiguationData":[TD([[makeQuery(id+"F0.imprint","INTERSECT",VERTEX,{"derivedFrom":[sQuery(id+"F0.wireOp",EDGE,"E2.2"),subQ0]}),1.0]])],"derivedFrom":subQ0})])],"isStart":true});}
            var Q19;
            Q19=makeQuery(id+"F1.opExtrude","CAP_EDGE",EDGE,{"disambiguationData":[OSD([sQuery(id+"F0.wireOp",EDGE,"E3.0")])],"isStart":true});
            var Q20;
            {var subQ0=sQuery(id+"F0.wireOp",EDGE,"E3.0");var subQ1=sQuery(id+"F0.wireOp",EDGE,"E2.2");Q20=makeQuery(id+"F3.opChamfer","BLEND_EDGE",EDGE,{"blendedFrom":[makeQuery(id+"F1.opExtrude","SWEPT_EDGE",EDGE,{"disambiguationData":[OSD([subQ1,subQ0])]}),makeQuery(id+"F1.opExtrude","CAP_FACE",FACE,{"disambiguationData":[OSD([sQuery(id+"F0.wireOp",EDGE,"E0"),sQuery(id+"F0.wireOp",EDGE,"E1.0"),sQuery(id+"F0.wireOp",EDGE,"E1.1"),sQuery(id+"F0.wireOp",EDGE,"E1.2"),sQuery(id+"F0.wireOp",EDGE,"E2.0"),sQuery(id+"F0.wireOp",EDGE,"E2.1"),subQ1,subQ0,sQuery(id+"F0.wireOp",EDGE,"E3.1"),sQuery(id+"F0.wireOp",EDGE,"E3.2"),sQuery(id+"F0.wireOp",EDGE,"E4.0"),sQuery(id+"F0.wireOp",EDGE,"E4.1"),sQuery(id+"F0.wireOp",EDGE,"E4.2"),sQuery(id+"F0.wireOp",EDGE,"E5.0"),sQuery(id+"F0.wireOp",EDGE,"E5.1"),sQuery(id+"F0.wireOp",EDGE,"E5.2"),sQuery(id+"F0.wireOp",EDGE,"E6.0"),sQuery(id+"F0.wireOp",EDGE,"E6.1"),sQuery(id+"F0.wireOp",EDGE,"E6.2")])],"isStart":true})],"blendedInto":[makeQuery(id+"F1.opExtrude","CAP_FACE",FACE,{"disambiguationData":[OSD([sQuery(id+"F0.wireOp",EDGE,"E0"),sQuery(id+"F0.wireOp",EDGE,"E1.0"),sQuery(id+"F0.wireOp",EDGE,"E1.1"),sQuery(id+"F0.wireOp",EDGE,"E1.2"),sQuery(id+"F0.wireOp",EDGE,"E2.0"),sQuery(id+"F0.wireOp",EDGE,"E2.1"),subQ1,subQ0,sQuery(id+"F0.wireOp",EDGE,"E3.1"),sQuery(id+"F0.wireOp",EDGE,"E3.2"),sQuery(id+"F0.wireOp",EDGE,"E4.0"),sQuery(id+"F0.wireOp",EDGE,"E4.1"),sQuery(id+"F0.wireOp",EDGE,"E4.2"),sQuery(id+"F0.wireOp",EDGE,"E5.0"),sQuery(id+"F0.wireOp",EDGE,"E5.1"),sQuery(id+"F0.wireOp",EDGE,"E5.2"),sQuery(id+"F0.wireOp",EDGE,"E6.0"),sQuery(id+"F0.wireOp",EDGE,"E6.1"),sQuery(id+"F0.wireOp",EDGE,"E6.2")])],"isStart":true})]});}
            var Q21;
            {var subQ0=sQuery(id+"F0.wireOp",EDGE,"E2.2");Q21=makeQuery(id+"F1.opExtrude","CAP_EDGE",EDGE,{"disambiguationData":[OSD([subQ0]),TDD([makeQuery(id+"F0.imprint","IMPRINT",EDGE,{"disambiguationData":[TD([[makeQuery(id+"F0.imprint","INTERSECT",VERTEX,{"derivedFrom":[subQ0,sQuery(id+"F0.wireOp",EDGE,"E3.0")]}),-1.0]])],"derivedFrom":subQ0})])],"isStart":true});}
            var Q22;
            {var subQ0=sQuery(id+"F0.wireOp",EDGE,"E6.0");Q22=makeQuery(id+"F1.opExtrude","CAP_EDGE",EDGE,{"disambiguationData":[OSD([subQ0]),TDD([makeQuery(id+"F0.imprint","IMPRINT",EDGE,{"disambiguationData":[TD([[makeQuery(id+"F0.imprint","INTERSECT",VERTEX,{"derivedFrom":[subQ0,sQuery(id+"F0.wireOp",EDGE,"E6.1")]}),1.0]])],"derivedFrom":subQ0})])],"isStart":true});}
            var Q23;
            Q23=makeQuery(id+"F1.opExtrude","CAP_EDGE",EDGE,{"disambiguationData":[OSD([sQuery(id+"F0.wireOp",EDGE,"E1.0")])],"isStart":true});
            var Q24;
            {var subQ0=sQuery(id+"F0.wireOp",EDGE,"E2.2");Q24=makeQuery(id+"F1.opExtrude","CAP_EDGE",EDGE,{"disambiguationData":[OSD([subQ0]),TDD([makeQuery(id+"F0.imprint","IMPRINT",EDGE,{"disambiguationData":[TD([[makeQuery(id+"F0.imprint","INTERSECT",VERTEX,{"derivedFrom":[sQuery(id+"F0.wireOp",EDGE,"E1.0"),subQ0]}),1.0]])],"derivedFrom":subQ0})])],"isStart":true});}
            var Q25;
            {var subQ0=sQuery(id+"F0.wireOp",EDGE,"E2.2");var subQ1=makeQuery(id+"F0.imprint","INTERSECT",VERTEX,{"derivedFrom":[sQuery(id+"F0.wireOp",EDGE,"E0"),subQ0]});Q25=makeQuery(id+"F1.opExtrude","CAP_EDGE",EDGE,{"disambiguationData":[OSD([subQ0]),TDD([makeQuery(id+"F0.imprint","IMPRINT",EDGE,{"disambiguationData":[TD([[makeQuery(id+"F0.imprint","INTERSECT",VERTEX,{"derivedFrom":[sQuery(id+"F0.wireOp",EDGE,"E2.1"),subQ0]}),-1.0]])],"derivedFrom":subQ0}),makeQuery(id+"F0.imprint","IMPRINT",EDGE,{"disambiguationData":[TD([[subQ1,-1.0]])],"derivedFrom":subQ0})])],"isStart":true});}
            var Q26;
            {var subQ0=sQuery(id+"F0.wireOp",EDGE,"E2.2");var subQ1=sQuery(id+"F0.wireOp",EDGE,"E2.1");Q26=makeQuery(id+"F3.opChamfer","BLEND_EDGE",EDGE,{"blendedFrom":[makeQuery(id+"F1.opExtrude","SWEPT_EDGE",EDGE,{"disambiguationData":[OSD([subQ1,subQ0])]}),makeQuery(id+"F1.opExtrude","CAP_FACE",FACE,{"disambiguationData":[OSD([sQuery(id+"F0.wireOp",EDGE,"E0"),sQuery(id+"F0.wireOp",EDGE,"E1.0"),sQuery(id+"F0.wireOp",EDGE,"E1.1"),sQuery(id+"F0.wireOp",EDGE,"E1.2"),sQuery(id+"F0.wireOp",EDGE,"E2.0"),subQ1,subQ0,sQuery(id+"F0.wireOp",EDGE,"E3.0"),sQuery(id+"F0.wireOp",EDGE,"E3.1"),sQuery(id+"F0.wireOp",EDGE,"E3.2"),sQuery(id+"F0.wireOp",EDGE,"E4.0"),sQuery(id+"F0.wireOp",EDGE,"E4.1"),sQuery(id+"F0.wireOp",EDGE,"E4.2"),sQuery(id+"F0.wireOp",EDGE,"E5.0"),sQuery(id+"F0.wireOp",EDGE,"E5.1"),sQuery(id+"F0.wireOp",EDGE,"E5.2"),sQuery(id+"F0.wireOp",EDGE,"E6.0"),sQuery(id+"F0.wireOp",EDGE,"E6.1"),sQuery(id+"F0.wireOp",EDGE,"E6.2")])],"isStart":true})],"blendedInto":[makeQuery(id+"F1.opExtrude","CAP_FACE",FACE,{"disambiguationData":[OSD([sQuery(id+"F0.wireOp",EDGE,"E0"),sQuery(id+"F0.wireOp",EDGE,"E1.0"),sQuery(id+"F0.wireOp",EDGE,"E1.1"),sQuery(id+"F0.wireOp",EDGE,"E1.2"),sQuery(id+"F0.wireOp",EDGE,"E2.0"),subQ1,subQ0,sQuery(id+"F0.wireOp",EDGE,"E3.0"),sQuery(id+"F0.wireOp",EDGE,"E3.1"),sQuery(id+"F0.wireOp",EDGE,"E3.2"),sQuery(id+"F0.wireOp",EDGE,"E4.0"),sQuery(id+"F0.wireOp",EDGE,"E4.1"),sQuery(id+"F0.wireOp",EDGE,"E4.2"),sQuery(id+"F0.wireOp",EDGE,"E5.0"),sQuery(id+"F0.wireOp",EDGE,"E5.1"),sQuery(id+"F0.wireOp",EDGE,"E5.2"),sQuery(id+"F0.wireOp",EDGE,"E6.0"),sQuery(id+"F0.wireOp",EDGE,"E6.1"),sQuery(id+"F0.wireOp",EDGE,"E6.2")])],"isStart":true})]});}
            var Q27;
            {var subQ0=sQuery(id+"F0.wireOp",EDGE,"E4.2");var subQ1=sQuery(id+"F0.wireOp",EDGE,"E2.2");Q27=makeQuery(id+"F3.opChamfer","BLEND_EDGE",EDGE,{"blendedFrom":[makeQuery(id+"F1.opExtrude","SWEPT_EDGE",EDGE,{"disambiguationData":[OSD([subQ1,subQ0])]}),makeQuery(id+"F1.opExtrude","CAP_FACE",FACE,{"disambiguationData":[OSD([sQuery(id+"F0.wireOp",EDGE,"E0"),sQuery(id+"F0.wireOp",EDGE,"E1.0"),sQuery(id+"F0.wireOp",EDGE,"E1.1"),sQuery(id+"F0.wireOp",EDGE,"E1.2"),sQuery(id+"F0.wireOp",EDGE,"E2.0"),sQuery(id+"F0.wireOp",EDGE,"E2.1"),subQ1,sQuery(id+"F0.wireOp",EDGE,"E3.0"),sQuery(id+"F0.wireOp",EDGE,"E3.1"),sQuery(id+"F0.wireOp",EDGE,"E3.2"),sQuery(id+"F0.wireOp",EDGE,"E4.0"),sQuery(id+"F0.wireOp",EDGE,"E4.1"),subQ0,sQuery(id+"F0.wireOp",EDGE,"E5.0"),sQuery(id+"F0.wireOp",EDGE,"E5.1"),sQuery(id+"F0.wireOp",EDGE,"E5.2"),sQuery(id+"F0.wireOp",EDGE,"E6.0"),sQuery(id+"F0.wireOp",EDGE,"E6.1"),sQuery(id+"F0.wireOp",EDGE,"E6.2")])],"isStart":true})],"blendedInto":[makeQuery(id+"F1.opExtrude","CAP_FACE",FACE,{"disambiguationData":[OSD([sQuery(id+"F0.wireOp",EDGE,"E0"),sQuery(id+"F0.wireOp",EDGE,"E1.0"),sQuery(id+"F0.wireOp",EDGE,"E1.1"),sQuery(id+"F0.wireOp",EDGE,"E1.2"),sQuery(id+"F0.wireOp",EDGE,"E2.0"),sQuery(id+"F0.wireOp",EDGE,"E2.1"),subQ1,sQuery(id+"F0.wireOp",EDGE,"E3.0"),sQuery(id+"F0.wireOp",EDGE,"E3.1"),sQuery(id+"F0.wireOp",EDGE,"E3.2"),sQuery(id+"F0.wireOp",EDGE,"E4.0"),sQuery(id+"F0.wireOp",EDGE,"E4.1"),subQ0,sQuery(id+"F0.wireOp",EDGE,"E5.0"),sQuery(id+"F0.wireOp",EDGE,"E5.1"),sQuery(id+"F0.wireOp",EDGE,"E5.2"),sQuery(id+"F0.wireOp",EDGE,"E6.0"),sQuery(id+"F0.wireOp",EDGE,"E6.1"),sQuery(id+"F0.wireOp",EDGE,"E6.2")])],"isStart":true})]});}
            var Q28;
            Q28=makeQuery(id+"F1.opExtrude","CAP_EDGE",EDGE,{"disambiguationData":[OSD([sQuery(id+"F0.wireOp",EDGE,"E2.1")])],"isStart":true});
            var Q29;
            {var subQ0=sQuery(id+"F0.wireOp",EDGE,"E4.2");var subQ1=sQuery(id+"F0.wireOp",EDGE,"E2.1");Q29=makeQuery(id+"F2.opFillet","BLEND_EDGE",EDGE,{"blendedFrom":[makeQuery(id+"F1.opExtrude","SWEPT_EDGE",EDGE,{"disambiguationData":[OSD([subQ1,subQ0])]}),makeQuery(id+"F1.opExtrude","CAP_FACE",FACE,{"disambiguationData":[OSD([sQuery(id+"F0.wireOp",EDGE,"E0"),sQuery(id+"F0.wireOp",EDGE,"E1.0"),sQuery(id+"F0.wireOp",EDGE,"E1.1"),sQuery(id+"F0.wireOp",EDGE,"E1.2"),sQuery(id+"F0.wireOp",EDGE,"E2.0"),subQ1,sQuery(id+"F0.wireOp",EDGE,"E2.2"),sQuery(id+"F0.wireOp",EDGE,"E3.0"),sQuery(id+"F0.wireOp",EDGE,"E3.1"),sQuery(id+"F0.wireOp",EDGE,"E3.2"),sQuery(id+"F0.wireOp",EDGE,"E4.0"),sQuery(id+"F0.wireOp",EDGE,"E4.1"),subQ0,sQuery(id+"F0.wireOp",EDGE,"E5.0"),sQuery(id+"F0.wireOp",EDGE,"E5.1"),sQuery(id+"F0.wireOp",EDGE,"E5.2"),sQuery(id+"F0.wireOp",EDGE,"E6.0"),sQuery(id+"F0.wireOp",EDGE,"E6.1"),sQuery(id+"F0.wireOp",EDGE,"E6.2")])],"isStart":true})],"blendedInto":[makeQuery(id+"F1.opExtrude","CAP_FACE",FACE,{"disambiguationData":[OSD([sQuery(id+"F0.wireOp",EDGE,"E0"),sQuery(id+"F0.wireOp",EDGE,"E1.0"),sQuery(id+"F0.wireOp",EDGE,"E1.1"),sQuery(id+"F0.wireOp",EDGE,"E1.2"),sQuery(id+"F0.wireOp",EDGE,"E2.0"),subQ1,sQuery(id+"F0.wireOp",EDGE,"E2.2"),sQuery(id+"F0.wireOp",EDGE,"E3.0"),sQuery(id+"F0.wireOp",EDGE,"E3.1"),sQuery(id+"F0.wireOp",EDGE,"E3.2"),sQuery(id+"F0.wireOp",EDGE,"E4.0"),sQuery(id+"F0.wireOp",EDGE,"E4.1"),subQ0,sQuery(id+"F0.wireOp",EDGE,"E5.0"),sQuery(id+"F0.wireOp",EDGE,"E5.1"),sQuery(id+"F0.wireOp",EDGE,"E5.2"),sQuery(id+"F0.wireOp",EDGE,"E6.0"),sQuery(id+"F0.wireOp",EDGE,"E6.1"),sQuery(id+"F0.wireOp",EDGE,"E6.2")])],"isStart":true})]});}
            var Q30;
            {var subQ0=sQuery(id+"F0.wireOp",EDGE,"E4.2");Q30=makeQuery(id+"F1.opExtrude","CAP_EDGE",EDGE,{"disambiguationData":[OSD([subQ0]),TDD([makeQuery(id+"F0.imprint","IMPRINT",EDGE,{"disambiguationData":[TD([[makeQuery(id+"F0.imprint","INTERSECT",VERTEX,{"derivedFrom":[sQuery(id+"F0.wireOp",EDGE,"E4.1"),subQ0]}),-1.0]])],"derivedFrom":subQ0})])],"isStart":true});}
            var Q31;
            {var subQ0=sQuery(id+"F0.wireOp",EDGE,"E4.1");Q31=makeQuery(id+"F1.opExtrude","CAP_EDGE",EDGE,{"disambiguationData":[OSD([subQ0]),TDD([makeQuery(id+"F0.imprint","IMPRINT",EDGE,{"disambiguationData":[TD([[makeQuery(id+"F0.imprint","INTERSECT",VERTEX,{"derivedFrom":[subQ0,sQuery(id+"F0.wireOp",EDGE,"E4.2")]}),1.0]])],"derivedFrom":subQ0})])],"isStart":true});}
            var Q32;
            Q32=makeQuery(id+"F1.opExtrude","CAP_EDGE",EDGE,{"disambiguationData":[OSD([sQuery(id+"F0.wireOp",EDGE,"E5.1")])],"isStart":true});
            var Q33;
            Q33=makeQuery(id+"F1.opExtrude","SWEPT_EDGE",EDGE,{"disambiguationData":[OSD([sQuery(id+"F0.wireOp",EDGE,"E3.1"),sQuery(id+"F0.wireOp",EDGE,"E3.2")])]});
            var Q34;
            Q34=makeQuery(id+"F1.opExtrude","SWEPT_EDGE",EDGE,{"disambiguationData":[OSD([sQuery(id+"F0.wireOp",EDGE,"E4.0"),sQuery(id+"F0.wireOp",EDGE,"E4.2")])]});
            chamfer(context, id + "F4", {"entities" : qUnion([Q0, Q1, Q2, Q3, Q4, Q5, Q6, Q7, Q8, Q9, Q10, Q11, Q12, Q13, Q14, Q15, Q16, Q17, Q18, Q19, Q20, Q21, Q22, Q23, Q24, Q25, Q26, Q27, Q28, Q29, Q30, Q31, Q32, Q33, Q34]), "width" : 1 * mm, "tangentPropagation" : true});
        }
        {
            var Q0;
            {var subQ0=sQuery(id+"F0.wireOp",EDGE,"E6.0");Q0=makeQuery(id+"F1.opExtrude","CAP_EDGE",EDGE,{"disambiguationData":[OSD([subQ0]),TDD([makeQuery(id+"F0.imprint","IMPRINT",EDGE,{"disambiguationData":[TD([[makeQuery(id+"F0.imprint","INTERSECT",VERTEX,{"derivedFrom":[sQuery(id+"F0.wireOp",EDGE,"E3.1"),subQ0]}),-1.0]])],"derivedFrom":subQ0})])],"isStart":true});}
            var Q1;
            {var subQ0=sQuery(id+"F0.wireOp",EDGE,"E3.1");Q1=makeQuery(id+"F1.opExtrude","CAP_EDGE",EDGE,{"disambiguationData":[OSD([subQ0]),TDD([makeQuery(id+"F0.imprint","IMPRINT",EDGE,{"disambiguationData":[TD([[makeQuery(id+"F0.imprint","INTERSECT",VERTEX,{"derivedFrom":[subQ0,sQuery(id+"F0.wireOp",EDGE,"E5.1")]}),-1.0]])],"derivedFrom":subQ0})])],"isStart":true});}
            var Q2;
            {var subQ0=sQuery(id+"F0.wireOp",EDGE,"E5.1");var subQ1=sQuery(id+"F0.wireOp",EDGE,"E3.1");Q2=makeQuery(id+"F4.opChamfer","BLEND_EDGE",EDGE,{"blendedFrom":[makeQuery(id+"F1.opExtrude","CAP_EDGE",EDGE,{"disambiguationData":[OSD([subQ0])],"isStart":true}),makeQuery(id+"F1.opExtrude","SWEPT_FACE",FACE,{"disambiguationData":[OSD([subQ1]),TDD([makeQuery(id+"F0.imprint","IMPRINT",EDGE,{"disambiguationData":[TD([[makeQuery(id+"F0.imprint","INTERSECT",VERTEX,{"derivedFrom":[subQ1,subQ0]}),-1.0]])],"derivedFrom":subQ1})])]})],"blendedInto":[makeQuery(id+"F1.opExtrude","SWEPT_FACE",FACE,{"disambiguationData":[OSD([subQ1]),TDD([makeQuery(id+"F0.imprint","IMPRINT",EDGE,{"disambiguationData":[TD([[makeQuery(id+"F0.imprint","INTERSECT",VERTEX,{"derivedFrom":[subQ1,subQ0]}),-1.0]])],"derivedFrom":subQ1})])]})]});}
            var Q3;
            {var subQ0=sQuery(id+"F0.wireOp",EDGE,"E4.2");Q3=makeQuery(id+"F1.opExtrude","CAP_EDGE",EDGE,{"disambiguationData":[OSD([subQ0]),TDD([makeQuery(id+"F0.imprint","IMPRINT",EDGE,{"disambiguationData":[TD([[makeQuery(id+"F0.imprint","INTERSECT",VERTEX,{"derivedFrom":[sQuery(id+"F0.wireOp",EDGE,"E2.2"),subQ0]}),-1.0]])],"derivedFrom":subQ0})])],"isStart":true});}
            var Q4;
            {var subQ0=sQuery(id+"F0.wireOp",EDGE,"E3.2");Q4=makeQuery(id+"F1.opExtrude","CAP_EDGE",EDGE,{"disambiguationData":[OSD([subQ0]),TDD([makeQuery(id+"F0.imprint","IMPRINT",EDGE,{"disambiguationData":[TD([[makeQuery(id+"F0.imprint","INTERSECT",VERTEX,{"derivedFrom":[sQuery(id+"F0.wireOp",EDGE,"E3.0"),subQ0]}),1.0]])],"derivedFrom":subQ0})])],"isStart":true});}
            chamfer(context, id + "F5", {"entities" : qUnion([Q0, Q1, Q2, Q3, Q4]), "width" : 0.5 * mm, "tangentPropagation" : true});
        }
    });
